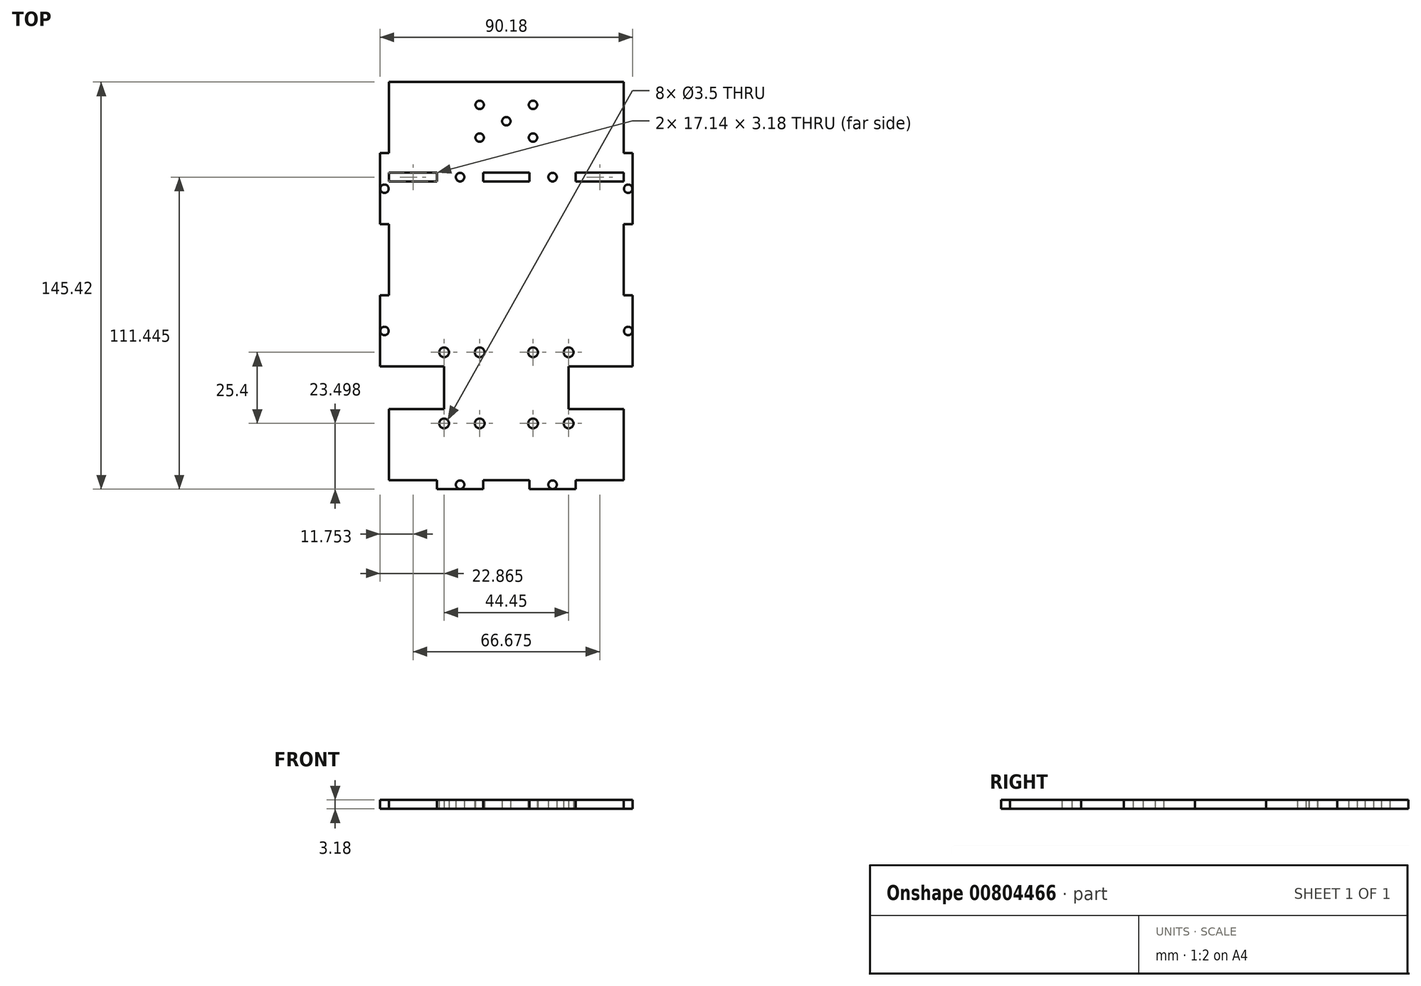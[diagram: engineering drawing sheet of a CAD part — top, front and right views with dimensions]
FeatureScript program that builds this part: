
annotation { "Feature Type Name" : "Feature", "Feature Type Description" : "" }
export const myFeature = defineFeature(function(context is Context, id is Id, definition is map)
    precondition{}
    {
        {
            var Q0;
            Q0=qCreatedBy(makeId("Top.planeOp"),FACE);
            var sketch = newSketch(context, id + "F0", { "sketchPlane" : qUnion([Q0])});
            skPoint(sketch, "E0.middle", {"position": v(0, 0) * mm});
            skLineSegment(sketch, "E1", {"start": v(-45.09, 11.14) * mm, "end": v(-22.23, 11.14) * mm});
            skLineSegment(sketch, "E2", {"start": v(-22.22, 11.14) * mm, "end": v(-22.22, -4.1) * mm});
            skPoint(sketch, "E3", {"position": v(-22.23, 3.52) * mm});
            skLineSegment(sketch, "E4", {"start": v(-51.44, 3.52) * mm, "end": v(-22.23, 3.52) * mm, "construction": true});
            skCircle(sketch, "E5", {"center": v(-22.23, 16.22) * mm, "radius": 1.75 * mm});
            skCircle(sketch, "E6.MirrorC", {"center": v(-22.22, -9.18) * mm, "radius": 1.75 * mm});
            skLineSegment(sketch, "E7", {"start": v(24.77, -32.68) * mm, "end": v(24.77, -29.5) * mm});
            skLineSegment(sketch, "E8.1.0.0", {"start": v(8.26, -32.68) * mm, "end": v(8.25, -29.5) * mm});
            skLineSegment(sketch, "E8.direction1", {"start": v(24.77, -32.68) * mm, "end": v(8.25, -32.68) * mm, "construction": true});
            skLineSegment(sketch, "E9", {"start": v(41.91, -29.5) * mm, "end": v(24.77, -29.5) * mm});
            skLineSegment(sketch, "E10", {"start": v(8.26, -29.5) * mm, "end": v(-8.26, -29.5) * mm});
            skCircle(sketch, "E11", {"center": v(16.51, -31.09) * mm, "radius": 1.52 * mm});
            skLineSegment(sketch, "E12", {"start": v(24.77, -31.09) * mm, "end": v(16.51, -31.09) * mm, "construction": true});
            skLineSegment(sketch, "E13", {"start": v(16.51, -31.09) * mm, "end": v(8.26, -31.09) * mm, "construction": true});
            skLineSegment(sketch, "E14.MirrorCS", {"start": v(24.77, -29.5) * mm, "end": v(24.77, -32.68) * mm});
            skCircle(sketch, "E15", {"center": v(-9.53, 16.22) * mm, "radius": 1.75 * mm});
            skCircle(sketch, "E16.MirrorC", {"center": v(-9.52, -9.18) * mm, "radius": 1.75 * mm});
            skLineSegment(sketch, "E17", {"start": v(-22.22, -9.18) * mm, "end": v(-9.52, -9.18) * mm, "construction": true});
            skLineSegment(sketch, "E18", {"start": v(-22.23, 16.22) * mm, "end": v(-9.53, 16.22) * mm, "construction": true});
            skPoint(sketch, "E19.MirrorP", {"position": v(22.23, 3.52) * mm});
            skLineSegment(sketch, "E20.MirrorCS", {"start": v(22.23, 16.22) * mm, "end": v(9.52, 16.22) * mm, "construction": true});
            skLineSegment(sketch, "E21.MirrorCS", {"start": v(45.09, 11.14) * mm, "end": v(22.23, 11.14) * mm});
            skCircle(sketch, "E22.MirrorC", {"center": v(9.52, -9.18) * mm, "radius": 1.75 * mm});
            skLineSegment(sketch, "E23.MirrorCS", {"start": v(22.22, 11.14) * mm, "end": v(22.22, -4.1) * mm});
            skCircle(sketch, "E24.MirrorC", {"center": v(9.52, 16.22) * mm, "radius": 1.75 * mm});
            skCircle(sketch, "E25.MirrorC", {"center": v(22.23, -9.18) * mm, "radius": 1.75 * mm});
            skCircle(sketch, "E26.MirrorC", {"center": v(22.23, 16.22) * mm, "radius": 1.75 * mm});
            skLineSegment(sketch, "E27.MirrorCS", {"start": v(51.44, 3.52) * mm, "end": v(22.23, 3.52) * mm, "construction": true});
            skLineSegment(sketch, "E28.MirrorCS", {"start": v(22.23, -9.18) * mm, "end": v(9.52, -9.18) * mm, "construction": true});
            skLineSegment(sketch, "E29", {"start": v(24.77, -32.68) * mm, "end": v(8.25, -32.68) * mm});
            skLineSegment(sketch, "E30.MirrorCS", {"start": v(-24.77, -29.5) * mm, "end": v(-24.77, -32.68) * mm});
            skLineSegment(sketch, "E31.MirrorCS", {"start": v(-24.77, -32.68) * mm, "end": v(-24.77, -29.5) * mm});
            skLineSegment(sketch, "E32.MirrorCS", {"start": v(-8.26, -32.68) * mm, "end": v(-8.26, -29.5) * mm});
            skLineSegment(sketch, "E33.MirrorCS", {"start": v(-24.77, -32.68) * mm, "end": v(-8.25, -32.68) * mm});
            skCircle(sketch, "E34.MirrorC", {"center": v(-16.51, -31.09) * mm, "radius": 1.52 * mm});
            skLineSegment(sketch, "E35.MirrorCS", {"start": v(-24.77, -31.09) * mm, "end": v(-16.51, -31.09) * mm, "construction": true});
            skLineSegment(sketch, "E36.MirrorCS", {"start": v(-16.51, -31.09) * mm, "end": v(-8.26, -31.09) * mm, "construction": true});
            skLineSegment(sketch, "E37.MirrorCS", {"start": v(-24.77, -32.68) * mm, "end": v(-8.25, -32.68) * mm, "construction": true});
            skLineSegment(sketch, "E38", {"start": v(41.91, -29.5) * mm, "end": v(41.91, -4.1) * mm});
            skLineSegment(sketch, "E39", {"start": v(41.91, -4.1) * mm, "end": v(22.22, -4.1) * mm});
            skLineSegment(sketch, "E40.MirrorCS", {"start": v(-41.91, -4.1) * mm, "end": v(-22.22, -4.1) * mm});
            skLineSegment(sketch, "E41.MirrorCS", {"start": v(-41.91, -29.5) * mm, "end": v(-41.91, -4.1) * mm});
            skLineSegment(sketch, "E42.MirrorCS", {"start": v(-41.91, -29.5) * mm, "end": v(-24.77, -29.5) * mm});
            skLineSegment(sketch, "E43", {"start": v(45.09, 36.54) * mm, "end": v(41.91, 36.54) * mm});
            skLineSegment(sketch, "E44", {"start": v(41.91, 36.54) * mm, "end": v(41.91, 61.94) * mm});
            skLineSegment(sketch, "E45", {"start": v(41.91, 61.94) * mm, "end": v(45.09, 61.94) * mm});
            skLineSegment(sketch, "E46", {"start": v(45.09, 11.14) * mm, "end": v(45.09, 36.54) * mm});
            skLineSegment(sketch, "E47.1.0.0", {"start": v(41.91, 87.34) * mm, "end": v(41.91, 112.74) * mm});
            skLineSegment(sketch, "E47.1.0.1", {"start": v(45.09, 61.94) * mm, "end": v(45.09, 87.34) * mm});
            skLineSegment(sketch, "E47.1.0.3", {"start": v(45.09, 87.34) * mm, "end": v(41.91, 87.34) * mm});
            skLineSegment(sketch, "E47.direction1", {"start": v(45.08, 11.14) * mm, "end": v(45.08, 61.94) * mm, "construction": true});
            skLineSegment(sketch, "E48.MirrorCS", {"start": v(-45.09, 36.54) * mm, "end": v(-41.91, 36.54) * mm});
            skLineSegment(sketch, "E49.MirrorCS", {"start": v(-41.91, 61.94) * mm, "end": v(-45.09, 61.94) * mm});
            skLineSegment(sketch, "E50.MirrorCS", {"start": v(-45.09, 87.34) * mm, "end": v(-41.91, 87.34) * mm});
            skLineSegment(sketch, "E51.MirrorCS", {"start": v(-45.08, 11.14) * mm, "end": v(-45.09, 36.54) * mm});
            skLineSegment(sketch, "E52.MirrorCS", {"start": v(-45.08, 11.14) * mm, "end": v(-45.08, 61.94) * mm, "construction": true});
            skLineSegment(sketch, "E53.MirrorCS", {"start": v(-41.91, 87.34) * mm, "end": v(-41.91, 112.74) * mm});
            skLineSegment(sketch, "E54.MirrorCS", {"start": v(-41.9, 36.54) * mm, "end": v(-41.91, 61.94) * mm});
            skLineSegment(sketch, "E55.MirrorCS", {"start": v(-45.09, 61.94) * mm, "end": v(-45.09, 87.34) * mm});
            skLineSegment(sketch, "E56", {"start": v(0, -29.5) * mm, "end": v(0, 77.18) * mm, "construction": true});
            skLineSegment(sketch, "E57", {"start": v(0, 23.84) * mm, "end": v(-56.76, 23.84) * mm, "construction": true});
            skCircle(sketch, "E58.MirrorC", {"center": v(-16.51, 78.77) * mm, "radius": 1.52 * mm});
            skCircle(sketch, "E59.MirrorC", {"center": v(16.51, 78.77) * mm, "radius": 1.52 * mm});
            skLineSegment(sketch, "E60.MirrorCS", {"start": v(-24.77, 80.35) * mm, "end": v(-24.77, 77.18) * mm});
            skLineSegment(sketch, "E61.MirrorCS", {"start": v(24.77, 80.35) * mm, "end": v(24.77, 77.18) * mm});
            skLineSegment(sketch, "E62.MirrorCS", {"start": v(-24.77, 77.18) * mm, "end": v(-24.77, 80.35) * mm});
            skLineSegment(sketch, "E63.MirrorCS", {"start": v(-8.26, 80.35) * mm, "end": v(-8.26, 77.18) * mm});
            skLineSegment(sketch, "E64.MirrorCS", {"start": v(24.77, 77.18) * mm, "end": v(24.77, 80.35) * mm});
            skLineSegment(sketch, "E65.MirrorCS", {"start": v(8.25, 80.35) * mm, "end": v(8.25, 77.18) * mm});
            skLineSegment(sketch, "E66.MirrorCS", {"start": v(8.25, 77.18) * mm, "end": v(-8.26, 77.18) * mm});
            skLineSegment(sketch, "E67.MirrorCS", {"start": v(-24.77, 78.77) * mm, "end": v(-16.51, 78.77) * mm, "construction": true});
            skLineSegment(sketch, "E68.MirrorCS", {"start": v(24.77, 78.77) * mm, "end": v(16.51, 78.77) * mm, "construction": true});
            skLineSegment(sketch, "E69.MirrorCS", {"start": v(-41.91, 77.18) * mm, "end": v(-24.77, 77.18) * mm});
            skLineSegment(sketch, "E70.MirrorCS", {"start": v(-16.51, 78.77) * mm, "end": v(-8.26, 78.77) * mm, "construction": true});
            skLineSegment(sketch, "E71.MirrorCS", {"start": v(41.91, 77.18) * mm, "end": v(24.77, 77.18) * mm});
            skLineSegment(sketch, "E72.MirrorCS", {"start": v(16.51, 78.77) * mm, "end": v(8.26, 78.77) * mm, "construction": true});
            skLineSegment(sketch, "E73", {"start": v(41.91, 77.18) * mm, "end": v(41.91, 80.35) * mm});
            skLineSegment(sketch, "E74", {"start": v(41.91, 80.35) * mm, "end": v(24.77, 80.35) * mm});
            skLineSegment(sketch, "E75", {"start": v(8.26, 80.35) * mm, "end": v(-8.26, 80.35) * mm});
            skLineSegment(sketch, "E76", {"start": v(-24.77, 80.35) * mm, "end": v(-41.91, 80.35) * mm});
            skLineSegment(sketch, "E77", {"start": v(-41.91, 80.35) * mm, "end": v(-41.91, 77.18) * mm});
            skLineSegment(sketch, "E78", {"start": v(41.91, 112.74) * mm, "end": v(-41.91, 112.74) * mm});
            skLineSegment(sketch, "E79", {"start": v(22.23, -9.18) * mm, "end": v(22.23, 16.22) * mm, "construction": true});
            skLineSegment(sketch, "E80", {"start": v(22.23, 3.52) * mm, "end": v(22.23, 3.52) * mm});
            skCircle(sketch, "E81", {"center": v(-43.5, 23.84) * mm, "radius": 1.5 * mm});
            skLineSegment(sketch, "E82", {"start": v(-43.5, 36.54) * mm, "end": v(-43.5, 23.84) * mm, "construction": true});
            skCircle(sketch, "E83", {"center": v(-43.5, 74.64) * mm, "radius": 1.5 * mm});
            skLineSegment(sketch, "E84", {"start": v(-43.5, 61.94) * mm, "end": v(-43.5, 74.64) * mm, "construction": true});
            skCircle(sketch, "E85.MirrorC", {"center": v(43.5, 23.84) * mm, "radius": 1.5 * mm});
            skCircle(sketch, "E86.MirrorC", {"center": v(43.5, 74.64) * mm, "radius": 1.5 * mm});
            skCircle(sketch, "E87", {"center": v(-9.53, 92.9) * mm, "radius": 1.5 * mm});
            skCircle(sketch, "E88", {"center": v(-9.53, 104.58) * mm, "radius": 1.5 * mm});
            skLineSegment(sketch, "E89", {"start": v(-9.53, 92.9) * mm, "end": v(-9.53, 104.58) * mm, "construction": true});
            skLineSegment(sketch, "E90.MirrorCS", {"start": v(9.52, 92.9) * mm, "end": v(9.52, 104.58) * mm, "construction": true});
            skCircle(sketch, "E91.MirrorC", {"center": v(9.53, 104.58) * mm, "radius": 1.5 * mm});
            skCircle(sketch, "E92.MirrorC", {"center": v(9.53, 92.9) * mm, "radius": 1.5 * mm});
            skLineSegment(sketch, "E93", {"start": v(-9.53, 92.9) * mm, "end": v(9.53, 104.58) * mm, "construction": true});
            skLineSegment(sketch, "E94", {"start": v(-9.53, 104.58) * mm, "end": v(9.53, 92.9) * mm, "construction": true});
            skCircle(sketch, "E95", {"center": v(0, 98.74) * mm, "radius": 1.5 * mm});
            skSolve(sketch);
        }
        {
            var Q0;
            Q0=makeQuery(id+"F0.imprint","IMPRINT",FACE,{"disambiguationData":[TD([[makeQuery(id+"F0.imprint","IMPRINT",EDGE,{"derivedFrom":sQuery(id+"F0.wireOp",EDGE,"E1")}),1.0]])]});
            extrude(context, id + "F1", {"entities" : qUnion([Q0]), "depth" : 3.17 * mm, "offsetDistance" : 25.4 * mm});
        }
    });
